# Revit family: 20.3 Глухая торцевая панель ANR P0
name_source: partatom
category: Оборудование
revit_build: Autodesk Revit 2016 (Build: 20161004_0715(x64)
units: mm (PartAtom-declared; Revit-internal decimal feet)

## family parameters
Всегда вертикально = Да
На основе рабочей плоскости = Нет
Общий = Нет
При загрузке вырезать с полостями = Нет
Размер круглого соединителя = Использовать диаметр
Тип детали = Нормальный
Точка расчета площади = Нет

## types (8) — shared parameters
Д = 150 мм
Д1 = 130 мм
Единица измерения = шт.
Завод изготовитель = KORF
Ключевая пометка = Вентиляция
Материал = Сталь серая
Наименование и тех.хар-ка = Глухая торцевая панель
Раздел = ОВ

## per-type parameters (varying)
| type | А | А2 | А3 | Б | Б2 | Б3 | Высота | Р | Середина | Ширина |
| ANR 6 P0 | 1000 мм | 1100 мм | 1080 мм | 495 мм | 1100 мм | 1080 мм | 446 мм | 25 мм | 248 мм | 951 мм |
| ANR 7 P0 | 1000 мм | 1100 мм | 1080 мм | 695 мм | 1320 мм | 1300 мм | 646 мм | 25 мм | 348 мм | 951 мм |
| ANR 8 P0 | 1220 мм | 1320 мм | 1300 мм | 695 мм | 1320 мм | 1300 мм | 635 мм | 30 мм | 348 мм | 1160 мм |
| ANR 12 P0 | 1335 мм | 1435 мм | 1415 мм | 810 мм | 1435 мм | 1415 мм | 744 мм | 33 мм | 405 мм | 1269 мм |
| ANR 20 P0 | 1560 мм | 1660 мм | 1640 мм | 1035 мм | 1660 мм | 1640 мм | 958 мм | 39 мм | 518 мм | 1483 мм |
| ANR 25 P0 | 1945 мм | 2045 мм | 2025 мм | 1420 мм | 2045 мм | 2025 мм | 1324 мм | 48 мм | 710 мм | 1849 мм |
| ANR 30 P0 | 2385 мм | 2485 мм | 2465 мм | 1420 мм | 2045 мм | 2025 мм | 1302 мм | 59 мм | 710 мм | 2267 мм |
| ANR 35 P0 | 2385 мм | 2485 мм | 2465 мм | 1860 мм | 2485 мм | 2465 мм | 1742 мм | 59 мм | 930 мм | 2267 мм |

note: column(s) folded — value = type name in every type: Тип, марка, обозначение
